# Revit family: ES-UCF3
name_source: partatom
category: Mechanical Equipment
revit_build: Autodesk Revit 2015 (Build: 20140606_1530(x64)
units: mm (PartAtom-declared; Revit-internal decimal feet)

## types (3) — shared parameters
Catalogue Pages = http://www.nuaire.info
Classification.Uniclass.Pr.Description = Fans
Classification.Uniclass.Pr.Number = Pr_65_67_29
Default Elevation = 1219 mm
Depth = 40 mm
Fax Number = +44(0)2920-858-222
Height = 75 mm
I&M Manual = http://nuaire.info
IFCExportAs = IfcFanType
Manufacturer = Nuaire
Manufacturer Name = Nuaire
Maximum Ambient Temperature = 40 °C
OmniClass Number = 23-33 31 19
OmniClass Title = Fans
Postcode = CF83 1NA
Revit Family Last Revised = 25/03/19
Telephone Number = +44(0)2920-858-200
URL = http://www.nuaire.co.uk
VAT Registration Number = 877308
Warranty Period = 3 Years
Weatherproof or Internal Only = Internal
Weight = 0.25 kg
Width = 163 mm

## per-type parameters (varying)
| type | Description | Type Comments | Unit Description | dial |
| ES-UCF | Wall Mounted Low Voltage Fan Speed Controller - Ventilation only | Wall Mounted Low Voltage Fan Speed Controller - Ventilation only | Wall Mounted Low Voltage Fan Speed Controller - Ventilation only | Yes |
| ES-UCFH | Wall Mounted Low Voltage Fan Speed Controller - Ventilation and Heating | Wall Mounted Low Voltage Fan Speed Controller - Ventilation and Heating | Wall Mounted Low Voltage Fan Speed Controller - Ventilation and Heating | No |
| ES-UCFHC | Wall Mounted Low Voltage Fan Speed Controller - Ventilation, Heating and Cooling | Wall Mounted Low Voltage Fan Speed Controller - Ventilation, Heating and Cooling | Wall Mounted Low Voltage Fan Speed Controller - Ventilation, Heating and Cooling | No |

note: column(s) folded — value = type name in every type: Model, Nuaire Model Code

## geometry (parser evidence)
native form markers: Blend x6, Sweep x2
no freeform markers — native parametric forms only
